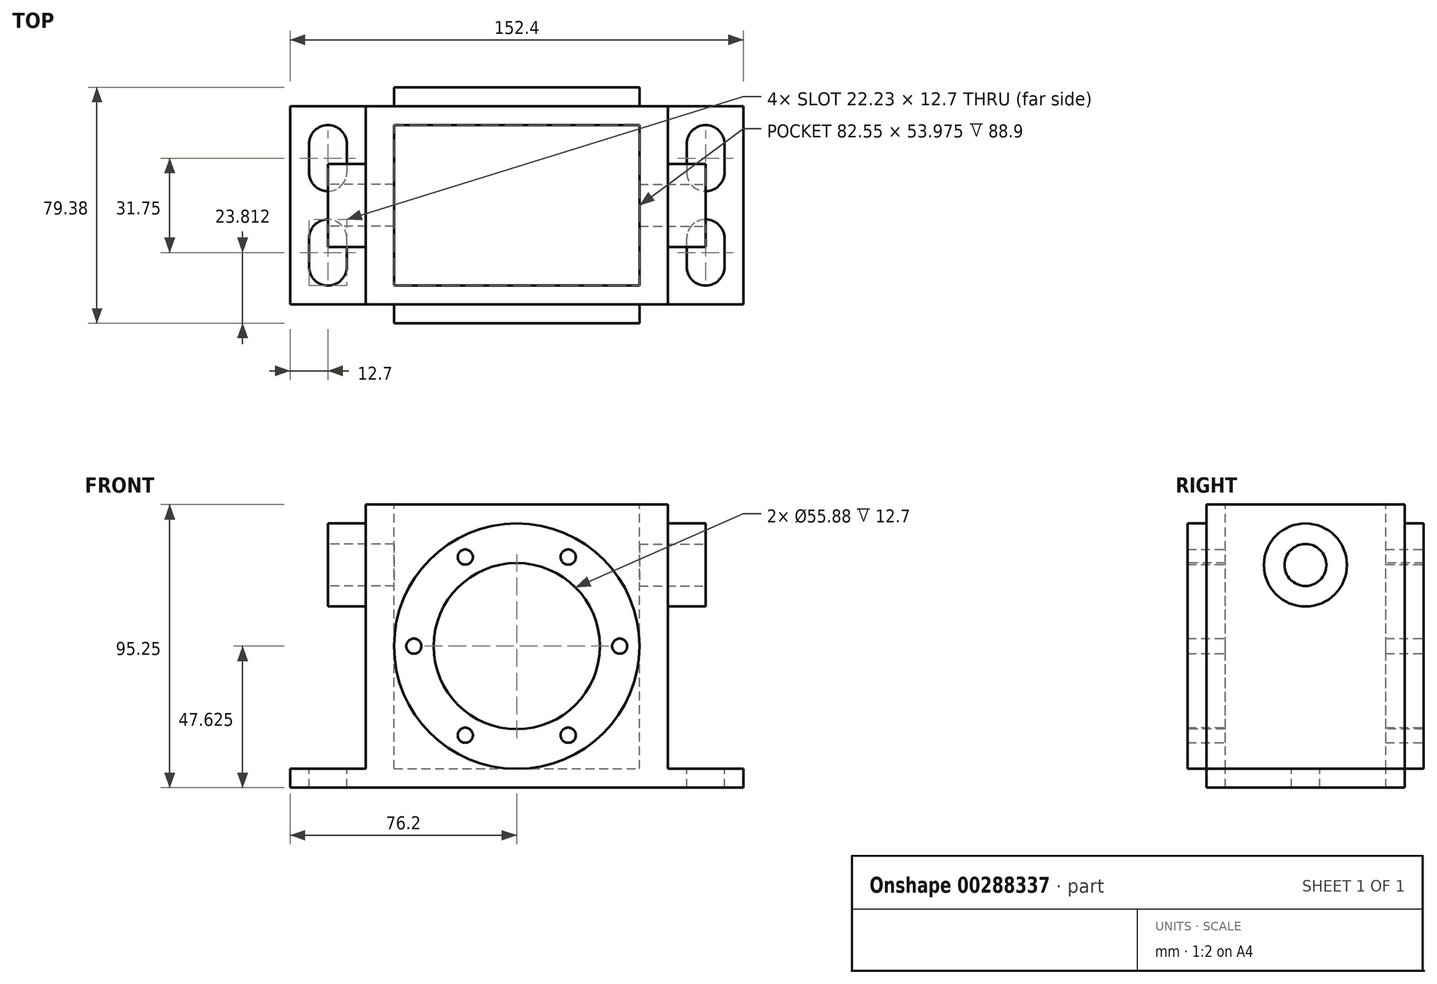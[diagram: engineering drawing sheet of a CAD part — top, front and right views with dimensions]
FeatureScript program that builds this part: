
annotation { "Feature Type Name" : "Feature", "Feature Type Description" : "" }
export const myFeature = defineFeature(function(context is Context, id is Id, definition is map)
    precondition{}
    {
        {
            var Q0;
            Q0=qCreatedBy(makeId("Top.planeOp"),FACE);
            var sketch = newSketch(context, id + "F0", { "sketchPlane" : qUnion([Q0])});
            skLineSegment(sketch, "E0.bottom", {"start": v(0, 0) * mm, "end": v(152.4, 0) * mm});
            skLineSegment(sketch, "E0.top", {"start": v(0, 66.68) * mm, "end": v(152.4, 66.68) * mm});
            skLineSegment(sketch, "E0.left", {"start": v(0, 0) * mm, "end": v(0, 66.68) * mm});
            skLineSegment(sketch, "E0.right", {"start": v(152.4, 0) * mm, "end": v(152.4, 66.68) * mm});
            skSolve(sketch);
        }
        {
            var Q0;
            Q0 = qSketchRegion(id + "F0", true);
            extrude(context, id + "F1", {"entities" : qUnion([Q0]), "depth" : 6.35 * mm});
        }
        {
            var Q0;
            Q0=makeQuery(id+"F1.opExtrude","CAP_FACE",FACE,{"disambiguationData":[OSD([sQuery(id+"F0.wireOp",EDGE,"E0.bottom"),sQuery(id+"F0.wireOp",EDGE,"E0.top"),sQuery(id+"F0.wireOp",EDGE,"E0.left"),sQuery(id+"F0.wireOp",EDGE,"E0.right")])],"isStart":false});
            var sketch = newSketch(context, id + "F2", { "sketchPlane" : qUnion([Q0])});
            skPoint(sketch, "E1", {"position": v(139.7, 53.98) * mm});
            skArc(sketch, "E2", {"start": v(146.05, 53.98) * mm, "mid": v(139.7, 60.33) * mm, "end": v(133.35, 53.98) * mm});
            skLineSegment(sketch, "E3", {"start": v(133.35, 53.98) * mm, "end": v(133.35, 44.45) * mm});
            skLineSegment(sketch, "E4", {"start": v(146.05, 53.98) * mm, "end": v(146.05, 44.45) * mm});
            skLineSegment(sketch, "E5", {"start": v(133.35, 44.45) * mm, "end": v(146.05, 44.45) * mm});
            skArc(sketch, "E6", {"start": v(133.35, 44.45) * mm, "mid": v(139.7, 38.1) * mm, "end": v(146.05, 44.45) * mm});
            skSolve(sketch);
        }
        {
            var Q0;
            Q0 = qSketchRegion(id + "F2", true);
            extrude(context, id + "F3", {"entities" : qUnion([Q0]), "operationType" : NewBodyOperationType.REMOVE, "endBound" : BoundingType.THROUGH_ALL, "oppositeDirection" : true, "depth" : 25.4 * mm});
        }
        {
            var Q0;
            Q0=makeQuery(id+"F1.opExtrude","CAP_FACE",FACE,{"disambiguationData":[OSD([sQuery(id+"F0.wireOp",EDGE,"E0.bottom"),sQuery(id+"F0.wireOp",EDGE,"E0.top"),sQuery(id+"F0.wireOp",EDGE,"E0.left"),sQuery(id+"F0.wireOp",EDGE,"E0.right")])],"isStart":false});
            var sketch = newSketch(context, id + "F4", { "sketchPlane" : qUnion([Q0])});
            skPoint(sketch, "E7", {"position": v(139.7, 0) * mm});
            skPoint(sketch, "E8", {"position": v(139.7, 12.7) * mm});
            skLineSegment(sketch, "E9", {"start": v(139.7, 12.7) * mm, "end": v(146.05, 12.7) * mm});
            skLineSegment(sketch, "E10", {"start": v(146.05, 12.7) * mm, "end": v(139.7, 12.7) * mm});
            skLineSegment(sketch, "E11", {"start": v(133.35, 12.7) * mm, "end": v(139.7, 12.7) * mm});
            skArc(sketch, "E12", {"start": v(133.35, 12.7) * mm, "mid": v(139.7, 6.35) * mm, "end": v(146.05, 12.7) * mm});
            skLineSegment(sketch, "E13", {"start": v(146.05, 12.7) * mm, "end": v(146.05, 22.23) * mm});
            skLineSegment(sketch, "E14", {"start": v(133.35, 12.7) * mm, "end": v(133.35, 22.23) * mm});
            skArc(sketch, "E15", {"start": v(146.05, 22.23) * mm, "mid": v(139.7, 28.57) * mm, "end": v(133.35, 22.23) * mm});
            skSolve(sketch);
        }
        {
            var Q0;
            Q0 = qSketchRegion(id + "F4", true);
            extrude(context, id + "F5", {"entities" : qUnion([Q0]), "operationType" : NewBodyOperationType.REMOVE, "endBound" : BoundingType.THROUGH_ALL, "oppositeDirection" : true, "depth" : 25.4 * mm});
        }
        {
            var Q0;
            Q0=makeQuery(id+"F1.opExtrude","CAP_FACE",FACE,{"disambiguationData":[OSD([sQuery(id+"F0.wireOp",EDGE,"E0.bottom"),sQuery(id+"F0.wireOp",EDGE,"E0.top"),sQuery(id+"F0.wireOp",EDGE,"E0.left"),sQuery(id+"F0.wireOp",EDGE,"E0.right")])],"isStart":false});
            var sketch = newSketch(context, id + "F6", { "sketchPlane" : qUnion([Q0])});
            skPoint(sketch, "E16.positionSnap0", {"position": v(139.7, 60.33) * mm});
            skPoint(sketch, "E17", {"position": v(12.7, 66.68) * mm});
            skPoint(sketch, "E18", {"position": v(12.7, 53.98) * mm});
            skLineSegment(sketch, "E19", {"start": v(12.7, 53.98) * mm, "end": v(19.05, 53.98) * mm});
            skLineSegment(sketch, "E20", {"start": v(12.7, 53.98) * mm, "end": v(6.35, 53.98) * mm});
            skArc(sketch, "E21", {"start": v(19.05, 53.98) * mm, "mid": v(12.7, 60.33) * mm, "end": v(6.35, 53.98) * mm});
            skLineSegment(sketch, "E22", {"start": v(19.05, 53.98) * mm, "end": v(19.05, 44.45) * mm});
            skLineSegment(sketch, "E23", {"start": v(6.35, 53.98) * mm, "end": v(6.35, 44.45) * mm});
            skArc(sketch, "E24", {"start": v(6.35, 44.45) * mm, "mid": v(12.7, 38.1) * mm, "end": v(19.05, 44.45) * mm});
            skSolve(sketch);
        }
        {
            var Q0;
            Q0 = qSketchRegion(id + "F6", true);
            extrude(context, id + "F7", {"entities" : qUnion([Q0]), "operationType" : NewBodyOperationType.REMOVE, "endBound" : BoundingType.THROUGH_ALL, "oppositeDirection" : true, "depth" : 25.4 * mm});
        }
        {
            var Q0;
            Q0=makeQuery(id+"F1.opExtrude","CAP_FACE",FACE,{"disambiguationData":[OSD([sQuery(id+"F0.wireOp",EDGE,"E0.bottom"),sQuery(id+"F0.wireOp",EDGE,"E0.top"),sQuery(id+"F0.wireOp",EDGE,"E0.left"),sQuery(id+"F0.wireOp",EDGE,"E0.right")])],"isStart":false});
            var sketch = newSketch(context, id + "F8", { "sketchPlane" : qUnion([Q0])});
            skPoint(sketch, "E25", {"position": v(12.7, 0) * mm});
            skPoint(sketch, "E26", {"position": v(12.7, 12.7) * mm});
            skLineSegment(sketch, "E27", {"start": v(12.7, 12.7) * mm, "end": v(19.05, 12.7) * mm});
            skLineSegment(sketch, "E28", {"start": v(12.7, 12.7) * mm, "end": v(6.35, 12.7) * mm});
            skArc(sketch, "E29", {"start": v(6.35, 12.7) * mm, "mid": v(12.7, 6.35) * mm, "end": v(19.05, 12.7) * mm});
            skLineSegment(sketch, "E30", {"start": v(19.05, 12.7) * mm, "end": v(19.05, 22.23) * mm});
            skLineSegment(sketch, "E31", {"start": v(6.35, 12.7) * mm, "end": v(6.35, 22.23) * mm});
            skArc(sketch, "E32", {"start": v(19.05, 22.23) * mm, "mid": v(12.7, 28.58) * mm, "end": v(6.35, 22.23) * mm});
            skSolve(sketch);
        }
        {
            var Q0;
            Q0 = qSketchRegion(id + "F8", true);
            extrude(context, id + "F9", {"entities" : qUnion([Q0]), "operationType" : NewBodyOperationType.REMOVE, "endBound" : BoundingType.THROUGH_ALL, "oppositeDirection" : true, "depth" : 25.4 * mm});
        }
        {
            var Q0;
            Q0=makeQuery(id+"F1.opExtrude","CAP_FACE",FACE,{"disambiguationData":[OSD([sQuery(id+"F0.wireOp",EDGE,"E0.bottom"),sQuery(id+"F0.wireOp",EDGE,"E0.top"),sQuery(id+"F0.wireOp",EDGE,"E0.left"),sQuery(id+"F0.wireOp",EDGE,"E0.right")])],"isStart":false});
            var sketch = newSketch(context, id + "F10", { "sketchPlane" : qUnion([Q0])});
            skPoint(sketch, "E33", {"position": v(25.4, 60.33) * mm});
            skPoint(sketch, "E33.positionSnap0", {"position": v(12.7, 60.33) * mm});
            skLineSegment(sketch, "E34.bottom", {"start": v(25.4, 66.68) * mm, "end": v(127, 66.68) * mm});
            skLineSegment(sketch, "E34.top", {"start": v(25.4, 0) * mm, "end": v(127, 0) * mm});
            skLineSegment(sketch, "E34.left", {"start": v(25.4, 66.68) * mm, "end": v(25.4, 0) * mm});
            skLineSegment(sketch, "E34.right", {"start": v(127, 66.68) * mm, "end": v(127, 0) * mm});
            skSolve(sketch);
        }
        {
            var Q0;
            Q0 = qSketchRegion(id + "F10", true);
            extrude(context, id + "F11", {"entities" : qUnion([Q0]), "operationType" : NewBodyOperationType.ADD, "depth" : 88.9 * mm});
        }
        {
            var Q0;
            Q0=makeQuery(id+"F11.opExtrude","CAP_FACE",FACE,{"disambiguationData":[OSD([sQuery(id+"F10.wireOp",EDGE,"E34.bottom"),sQuery(id+"F10.wireOp",EDGE,"E34.top"),sQuery(id+"F10.wireOp",EDGE,"E34.left"),sQuery(id+"F10.wireOp",EDGE,"E34.right")])],"isStart":false});
            var sketch = newSketch(context, id + "F12", { "sketchPlane" : qUnion([Q0])});
            skPoint(sketch, "E35", {"position": v(25.4, 66.68) * mm});
            skPoint(sketch, "E36", {"position": v(34.93, 66.68) * mm});
            skPoint(sketch, "E37", {"position": v(34.93, 60.33) * mm});
            skPoint(sketch, "E38", {"position": v(25.4, 0) * mm});
            skPoint(sketch, "E39", {"position": v(34.93, 0) * mm});
            skPoint(sketch, "E40", {"position": v(34.93, 6.35) * mm});
            skLineSegment(sketch, "E41.bottom", {"start": v(34.93, 60.33) * mm, "end": v(117.47, 60.33) * mm});
            skLineSegment(sketch, "E41.top", {"start": v(34.93, 6.35) * mm, "end": v(117.47, 6.35) * mm});
            skLineSegment(sketch, "E41.left", {"start": v(34.93, 60.33) * mm, "end": v(34.93, 6.35) * mm});
            skLineSegment(sketch, "E41.right", {"start": v(117.47, 60.33) * mm, "end": v(117.47, 6.35) * mm});
            skSolve(sketch);
        }
        {
            var Q0;
            Q0 = qSketchRegion(id + "F12", true);
            extrude(context, id + "F13", {"entities" : qUnion([Q0]), "operationType" : NewBodyOperationType.REMOVE, "oppositeDirection" : true, "depth" : 88.9 * mm});
        }
        {
            var Q0;
            Q0=makeQuery(id+"F11.boolean.opBoolean","MERGE",FACE,{"derivedFrom":[makeQuery(id+"F1.opExtrude","SWEPT_FACE",FACE,{"disambiguationData":[OSD([sQuery(id+"F0.wireOp",EDGE,"E0.bottom")])]}),makeQuery(id+"F11.opExtrude","SWEPT_FACE",FACE,{"disambiguationData":[OSD([sQuery(id+"F10.wireOp",EDGE,"E34.top")])]})]});
            var sketch = newSketch(context, id + "F14", { "sketchPlane" : qUnion([Q0])});
            skPoint(sketch, "E42", {"position": v(76.2, 47.62) * mm});
            skPoint(sketch, "E42.positionSnap0", {"position": v(76.2, 95.25) * mm});
            skCircle(sketch, "E43", {"center": v(76.2, 47.62) * mm, "radius": 41.28 * mm});
            skSolve(sketch);
        }
        {
            var Q0;
            Q0 = qSketchRegion(id + "F14", true);
            extrude(context, id + "F15", {"entities" : qUnion([Q0]), "operationType" : NewBodyOperationType.ADD, "depth" : 6.35 * mm});
        }
        {
            var Q0;
            Q0=makeQuery(id+"F15.opExtrude","CAP_FACE",FACE,{"disambiguationData":[OSD([sQuery(id+"F14.wireOp",EDGE,"E43")])],"isStart":false});
            var sketch = newSketch(context, id + "F16", { "sketchPlane" : qUnion([Q0])});
            skCircle(sketch, "E44", {"center": v(76.2, 47.62) * mm, "radius": 27.94 * mm});
            skSolve(sketch);
        }
        {
            var Q0;
            Q0=makeQuery(id+"F11.boolean.opBoolean","MERGE",FACE,{"derivedFrom":[makeQuery(id+"F1.opExtrude","SWEPT_FACE",FACE,{"disambiguationData":[OSD([sQuery(id+"F0.wireOp",EDGE,"E0.top")])]}),makeQuery(id+"F11.opExtrude","SWEPT_FACE",FACE,{"disambiguationData":[OSD([sQuery(id+"F10.wireOp",EDGE,"E34.bottom")])]})]});
            var sketch = newSketch(context, id + "F17", { "sketchPlane" : qUnion([Q0])});
            skPoint(sketch, "E45", {"position": v(-76.2, 47.62) * mm});
            skPoint(sketch, "E45.positionSnap0", {"position": v(-76.2, 95.25) * mm});
            skCircle(sketch, "E46", {"center": v(-76.2, 47.62) * mm, "radius": 41.28 * mm});
            skSolve(sketch);
        }
        {
            var Q0;
            Q0 = qSketchRegion(id + "F17", true);
            extrude(context, id + "F18", {"entities" : qUnion([Q0]), "operationType" : NewBodyOperationType.ADD, "depth" : 6.35 * mm});
        }
        {
            var Q0;
            Q0=makeQuery(id+"F18.opExtrude","CAP_FACE",FACE,{"disambiguationData":[OSD([sQuery(id+"F17.wireOp",EDGE,"E46")])],"isStart":false});
            var sketch = newSketch(context, id + "F19", { "sketchPlane" : qUnion([Q0])});
            skCircle(sketch, "E47", {"center": v(-76.2, 47.62) * mm, "radius": 27.94 * mm});
            skCircle(sketch, "E48", {"center": v(-41.6, 47.62) * mm, "radius": 2.55 * mm});
            skCircle(sketch, "E49", {"center": v(-110.8, 47.62) * mm, "radius": 2.55 * mm});
            skCircle(sketch, "E50.1.0", {"center": v(-93.5, 17.65) * mm, "radius": 2.55 * mm});
            skCircle(sketch, "E50.2.0", {"center": v(-93.5, 77.6) * mm, "radius": 2.55 * mm});
            skLineSegment(sketch, "E50.anchor1", {"start": v(-76.2, 47.62) * mm, "end": v(-41.6, 47.62) * mm, "construction": true});
            skCircle(sketch, "E51.1.1", {"center": v(-58.9, 17.65) * mm, "radius": 2.55 * mm});
            skCircle(sketch, "E51.2.1", {"center": v(-58.9, 77.6) * mm, "radius": 2.55 * mm});
            skSolve(sketch);
        }
        {
            var Q0;
            Q0=makeQuery(id+"F19.imprint","IMPRINT",FACE,{"disambiguationData":[TD([[makeQuery(id+"F19.imprint","IMPRINT",EDGE,{"derivedFrom":sQuery(id+"F19.wireOp",EDGE,"E50.2.0")}),1.0]])]});
            var Q1;
            Q1=makeQuery(id+"F19.imprint","IMPRINT",FACE,{"disambiguationData":[TD([[makeQuery(id+"F19.imprint","IMPRINT",EDGE,{"derivedFrom":sQuery(id+"F19.wireOp",EDGE,"E50.1.0")}),1.0]])]});
            var Q2;
            Q2=makeQuery(id+"F19.imprint","IMPRINT",FACE,{"disambiguationData":[TD([[makeQuery(id+"F19.imprint","IMPRINT",EDGE,{"derivedFrom":sQuery(id+"F19.wireOp",EDGE,"E49")}),1.0]])]});
            var Q3;
            Q3=makeQuery(id+"F19.imprint","IMPRINT",FACE,{"disambiguationData":[TD([[makeQuery(id+"F19.imprint","IMPRINT",EDGE,{"derivedFrom":sQuery(id+"F19.wireOp",EDGE,"E51.1.1")}),1.0]])]});
            var Q4;
            Q4=makeQuery(id+"F19.imprint","IMPRINT",FACE,{"disambiguationData":[TD([[makeQuery(id+"F19.imprint","IMPRINT",EDGE,{"derivedFrom":sQuery(id+"F19.wireOp",EDGE,"E48")}),1.0]])]});
            var Q5;
            Q5=makeQuery(id+"F19.imprint","IMPRINT",FACE,{"disambiguationData":[TD([[makeQuery(id+"F19.imprint","IMPRINT",EDGE,{"derivedFrom":sQuery(id+"F19.wireOp",EDGE,"E51.2.1")}),1.0]])]});
            var Q6;
            Q6=sQuery(id+"F19.wireOp",EDGE,"E49");
            var Q7;
            Q7=sQuery(id+"F19.wireOp",EDGE,"E50.2.0");
            var Q8;
            Q8=sQuery(id+"F19.wireOp",EDGE,"E51.2.1");
            var Q9;
            Q9=sQuery(id+"F19.wireOp",EDGE,"E48");
            var Q10;
            Q10=sQuery(id+"F19.wireOp",EDGE,"E51.1.1");
            var Q11;
            Q11=sQuery(id+"F19.wireOp",EDGE,"E50.1.0");
            extrude(context, id + "F20", {"entities" : qUnion([Q0, Q1, Q2, Q3, Q4, Q5]), "operationType" : NewBodyOperationType.REMOVE, "surfaceEntities" : qUnion([Q6, Q7, Q8, Q9, Q10, Q11]), "endBound" : BoundingType.THROUGH_ALL, "oppositeDirection" : true, "depth" : 25.4 * mm});
        }
        {
            var Q0;
            Q0=makeQuery(id+"F16.imprint","IMPRINT",FACE,{"disambiguationData":[TD([[makeQuery(id+"F16.imprint","IMPRINT",EDGE,{"derivedFrom":sQuery(id+"F16.wireOp",EDGE,"E44")}),1.0]])]});
            extrude(context, id + "F21", {"entities" : qUnion([Q0]), "operationType" : NewBodyOperationType.REMOVE, "endBound" : BoundingType.THROUGH_ALL, "oppositeDirection" : true, "depth" : 25.4 * mm});
        }
        {
            var Q0;
            Q0=makeQuery(id+"F11.opExtrude","SWEPT_FACE",FACE,{"disambiguationData":[OSD([sQuery(id+"F10.wireOp",EDGE,"E34.left")])]});
            var sketch = newSketch(context, id + "F22", { "sketchPlane" : qUnion([Q0])});
            skCircle(sketch, "E52", {"center": v(-33.34, 74.93) * mm, "radius": 13.97 * mm});
            skPoint(sketch, "E53", {"position": v(-33.34, 95.25) * mm});
            skSolve(sketch);
        }
        {
            var Q0;
            Q0 = qSketchRegion(id + "F22", true);
            extrude(context, id + "F23", {"entities" : qUnion([Q0]), "operationType" : NewBodyOperationType.ADD, "depth" : 12.7 * mm});
        }
        {
            var Q0;
            Q0=makeQuery(id+"F23.opExtrude","CAP_FACE",FACE,{"disambiguationData":[OSD([sQuery(id+"F22.wireOp",EDGE,"E52")])],"isStart":false});
            var sketch = newSketch(context, id + "F24", { "sketchPlane" : qUnion([Q0])});
            skCircle(sketch, "E54", {"center": v(-33.34, 74.93) * mm, "radius": 7.05 * mm});
            skSolve(sketch);
        }
        {
            var Q0;
            Q0 = qSketchRegion(id + "F24", true);
            extrude(context, id + "F25", {"entities" : qUnion([Q0]), "operationType" : NewBodyOperationType.REMOVE, "oppositeDirection" : true, "depth" : 22.25 * mm});
        }
        {
            var Q0;
            Q0=makeQuery(id+"F11.opExtrude","SWEPT_FACE",FACE,{"disambiguationData":[OSD([sQuery(id+"F10.wireOp",EDGE,"E34.right")])]});
            var sketch = newSketch(context, id + "F26", { "sketchPlane" : qUnion([Q0])});
            skCircle(sketch, "E55", {"center": v(33.34, 74.93) * mm, "radius": 13.97 * mm});
            skSolve(sketch);
        }
        {
            var Q0;
            Q0 = qSketchRegion(id + "F26", true);
            extrude(context, id + "F27", {"entities" : qUnion([Q0]), "operationType" : NewBodyOperationType.ADD, "depth" : 12.7 * mm});
        }
        {
            var Q0;
            Q0=makeQuery(id+"F27.opExtrude","CAP_FACE",FACE,{"disambiguationData":[OSD([sQuery(id+"F26.wireOp",EDGE,"E55")])],"isStart":false});
            var sketch = newSketch(context, id + "F28", { "sketchPlane" : qUnion([Q0])});
            skCircle(sketch, "E56", {"center": v(33.34, 74.93) * mm, "radius": 7.05 * mm});
            skSolve(sketch);
        }
        {
            var Q0;
            Q0 = qSketchRegion(id + "F28", true);
            extrude(context, id + "F29", {"entities" : qUnion([Q0]), "operationType" : NewBodyOperationType.REMOVE, "oppositeDirection" : true, "depth" : 22.25 * mm});
        }
    });
